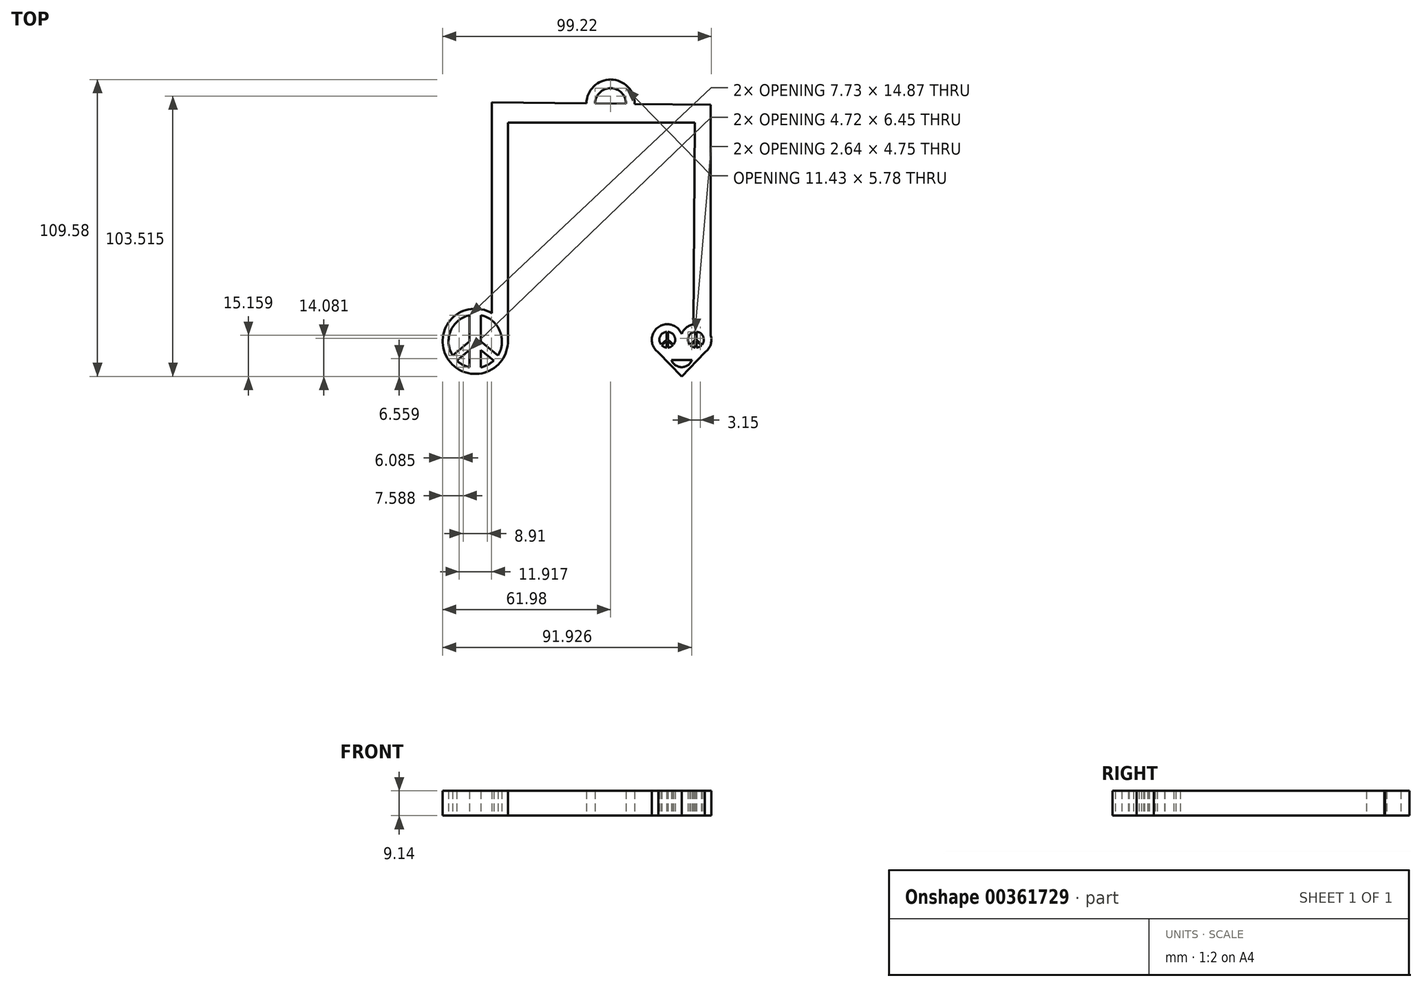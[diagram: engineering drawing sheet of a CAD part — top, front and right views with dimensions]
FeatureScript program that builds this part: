
annotation { "Feature Type Name" : "Feature", "Feature Type Description" : "" }
export const myFeature = defineFeature(function(context is Context, id is Id, definition is map)
    precondition{}
    {
        {
            var Q0;
            Q0=qCreatedBy(makeId("Top.planeOp"),FACE);
            var sketch = newSketch(context, id + "F0", { "sketchPlane" : qUnion([Q0])});
            skArc(sketch, "E0", {"start": v(34.84, -44.63) * mm, "mid": v(36.92, -41.86) * mm, "end": v(37.01, -38.4) * mm});
            skArc(sketch, "E1", {"start": v(26.23, -37.82) * mm, "mid": v(17.4, -35.5) * mm, "end": v(17.62, -44.63) * mm});
            skLineSegment(sketch, "E2", {"start": v(26.23, -53.53) * mm, "end": v(34.84, -44.63) * mm});
            skLineSegment(sketch, "E3", {"start": v(26.23, -53.53) * mm, "end": v(17.62, -44.63) * mm});
            skLineSegment(sketch, "E4", {"start": v(37.01, -23.14) * mm, "end": v(36.96, -23.14) * mm});
            skArc(sketch, "E5.trimOffspring", {"start": v(30.56, -34.35) * mm, "mid": v(27.95, -35.52) * mm, "end": v(26.23, -37.82) * mm});
            skLineSegment(sketch, "E6", {"start": v(-52.03, -50.2) * mm, "end": v(-52.03, -43.75) * mm});
            skLineSegment(sketch, "E7", {"start": v(-47.84, -50.2) * mm, "end": v(-47.84, -43.75) * mm});
            skLineSegment(sketch, "E8", {"start": v(-47.84, -40.56) * mm, "end": v(-41.6, -45.8) * mm});
            skLineSegment(sketch, "E9", {"start": v(-52.03, -40.56) * mm, "end": v(-58.28, -45.8) * mm});
            skLineSegment(sketch, "E10", {"start": v(-43.12, -47.68) * mm, "end": v(-47.84, -43.75) * mm});
            skLineSegment(sketch, "E11", {"start": v(-52.03, -43.75) * mm, "end": v(-56.75, -47.68) * mm});
            skLineSegment(sketch, "E12.trimOffspring", {"start": v(-47.84, -40.56) * mm, "end": v(-47.84, -30.93) * mm});
            skLineSegment(sketch, "E13.trimOffspring", {"start": v(-52.03, -40.56) * mm, "end": v(-52.03, -30.93) * mm});
            skArc(sketch, "E14", {"start": v(-52.03, -30.93) * mm, "mid": v(-59.02, -36.75) * mm, "end": v(-58.28, -45.8) * mm});
            skArc(sketch, "E15", {"start": v(-43.86, -30.17) * mm, "mid": v(-60.29, -46.72) * mm, "end": v(-37.9, -40.2) * mm});
            skLineSegment(sketch, "E16", {"start": v(-43.86, -30.17) * mm, "end": v(-43.86, 47.64) * mm});
            skArc(sketch, "E17.trimOffspring", {"start": v(-41.6, -45.8) * mm, "mid": v(-40.85, -36.75) * mm, "end": v(-47.84, -30.93) * mm});
            skArc(sketch, "E18.trimOffspring", {"start": v(-47.84, -50.2) * mm, "mid": v(-45.3, -49.27) * mm, "end": v(-43.12, -47.68) * mm});
            skArc(sketch, "E19.trimOffspring", {"start": v(-56.75, -47.68) * mm, "mid": v(-54.57, -49.27) * mm, "end": v(-52.03, -50.2) * mm});
            skLineSegment(sketch, "E20", {"start": v(37.01, -38.4) * mm, "end": v(37.01, 46.75) * mm});
            skArc(sketch, "E21", {"start": v(23.28, -41.73) * mm, "mid": v(23.61, -38.79) * mm, "end": v(21.2, -37.07) * mm});
            skArc(sketch, "E22", {"start": v(31.78, -42.9) * mm, "mid": v(32.72, -42.65) * mm, "end": v(33.53, -42.1) * mm});
            skLineSegment(sketch, "E23", {"start": v(26.23, -47.48) * mm, "end": v(30.04, -47.48) * mm});
            skLineSegment(sketch, "E24", {"start": v(26.23, -47.48) * mm, "end": v(22.42, -47.48) * mm});
            skArc(sketch, "E25", {"start": v(22.42, -47.48) * mm, "mid": v(26.23, -50.1) * mm, "end": v(30.04, -47.48) * mm});
            skLineSegment(sketch, "E26", {"start": v(37.01, 46.75) * mm, "end": v(8.89, 47.06) * mm});
            skArc(sketch, "E27", {"start": v(8.89, 47.06) * mm, "mid": v(0.1, 56.05) * mm, "end": v(-8.89, 47.26) * mm});
            skArc(sketch, "E28", {"start": v(5.71, 47.1) * mm, "mid": v(0.06, 52.87) * mm, "end": v(-5.71, 47.22) * mm});
            skLineSegment(sketch, "E29.trimOffspring", {"start": v(5.71, 47.1) * mm, "end": v(-5.71, 47.22) * mm});
            skLineSegment(sketch, "E30.trimOffspring", {"start": v(-8.89, 47.26) * mm, "end": v(-43.86, 47.64) * mm});
            skLineSegment(sketch, "E31", {"start": v(-37.9, -40.2) * mm, "end": v(-37.9, 40.2) * mm});
            skLineSegment(sketch, "E32", {"start": v(-37.9, 40.2) * mm, "end": v(31.1, 40.2) * mm});
            skLineSegment(sketch, "E33", {"start": v(30.56, -34.35) * mm, "end": v(31.1, 40.2) * mm});
            skPoint(sketch, "E34", {"position": v(26.23, -44.3) * mm});
            skLineSegment(sketch, "E35", {"start": v(20.7, -37.07) * mm, "end": v(20.7, -39.98) * mm});
            skLineSegment(sketch, "E36", {"start": v(21.2, -37.07) * mm, "end": v(21.2, -39.98) * mm});
            skLineSegment(sketch, "E37", {"start": v(23.28, -41.73) * mm, "end": v(21.2, -39.98) * mm});
            skLineSegment(sketch, "E38", {"start": v(18.6, -41.73) * mm, "end": v(20.7, -39.98) * mm});
            skLineSegment(sketch, "E39", {"start": v(21.2, -40.5) * mm, "end": v(23.03, -42.03) * mm});
            skLineSegment(sketch, "E40", {"start": v(20.7, -40.5) * mm, "end": v(18.89, -42.06) * mm});
            skLineSegment(sketch, "E41.trimOffspring", {"start": v(20.7, -40.5) * mm, "end": v(20.7, -42.9) * mm});
            skArc(sketch, "E42.trimOffspring", {"start": v(21.2, -42.9) * mm, "mid": v(22.2, -42.62) * mm, "end": v(23.03, -42.03) * mm});
            skArc(sketch, "E43.trimOffspring", {"start": v(18.89, -42.06) * mm, "mid": v(19.72, -42.63) * mm, "end": v(20.7, -42.9) * mm});
            skArc(sketch, "E44.trimOffspring", {"start": v(20.7, -37.07) * mm, "mid": v(18.28, -38.79) * mm, "end": v(18.6, -41.73) * mm});
            skLineSegment(sketch, "E45.trimOffspring", {"start": v(21.2, -40.5) * mm, "end": v(21.2, -42.9) * mm});
            skLineSegment(sketch, "E46", {"start": v(31.27, -37.07) * mm, "end": v(31.27, -39.98) * mm});
            skLineSegment(sketch, "E47", {"start": v(31.78, -37.07) * mm, "end": v(31.78, -39.98) * mm});
            skLineSegment(sketch, "E48", {"start": v(31.27, -39.98) * mm, "end": v(29.26, -41.83) * mm});
            skLineSegment(sketch, "E49", {"start": v(33.79, -41.83) * mm, "end": v(31.78, -39.98) * mm});
            skLineSegment(sketch, "E50", {"start": v(31.27, -40.5) * mm, "end": v(29.51, -42.1) * mm});
            skLineSegment(sketch, "E51", {"start": v(33.53, -42.1) * mm, "end": v(31.78, -40.5) * mm});
            skArc(sketch, "E52.trimOffspring", {"start": v(33.79, -41.83) * mm, "mid": v(34.21, -38.84) * mm, "end": v(31.78, -37.07) * mm});
            skArc(sketch, "E53.trimOffspring", {"start": v(31.27, -37.07) * mm, "mid": v(28.83, -38.84) * mm, "end": v(29.26, -41.83) * mm});
            skArc(sketch, "E54.trimOffspring", {"start": v(29.51, -42.1) * mm, "mid": v(30.32, -42.65) * mm, "end": v(31.27, -42.9) * mm});
            skLineSegment(sketch, "E55.trimOffspring", {"start": v(31.27, -40.5) * mm, "end": v(31.27, -42.9) * mm});
            skLineSegment(sketch, "E56.trimOffspring", {"start": v(31.78, -40.5) * mm, "end": v(31.78, -42.9) * mm});
            skSolve(sketch);
        }
        {
            var Q0;
            {var subQ3=sQuery(id+"F0.wireOp",EDGE,"E0");Q0=makeQuery(id+"F0.imprint","IMPRINT",FACE,{"disambiguationData":[TD([[makeQuery(id+"F0.imprint","IMPRINT",EDGE,{"derivedFrom":subQ3}),1.0]])]});}
            extrude(context, id + "F1", {"entities" : qUnion([Q0]), "depth" : 9.14 * mm});
        }
    });
